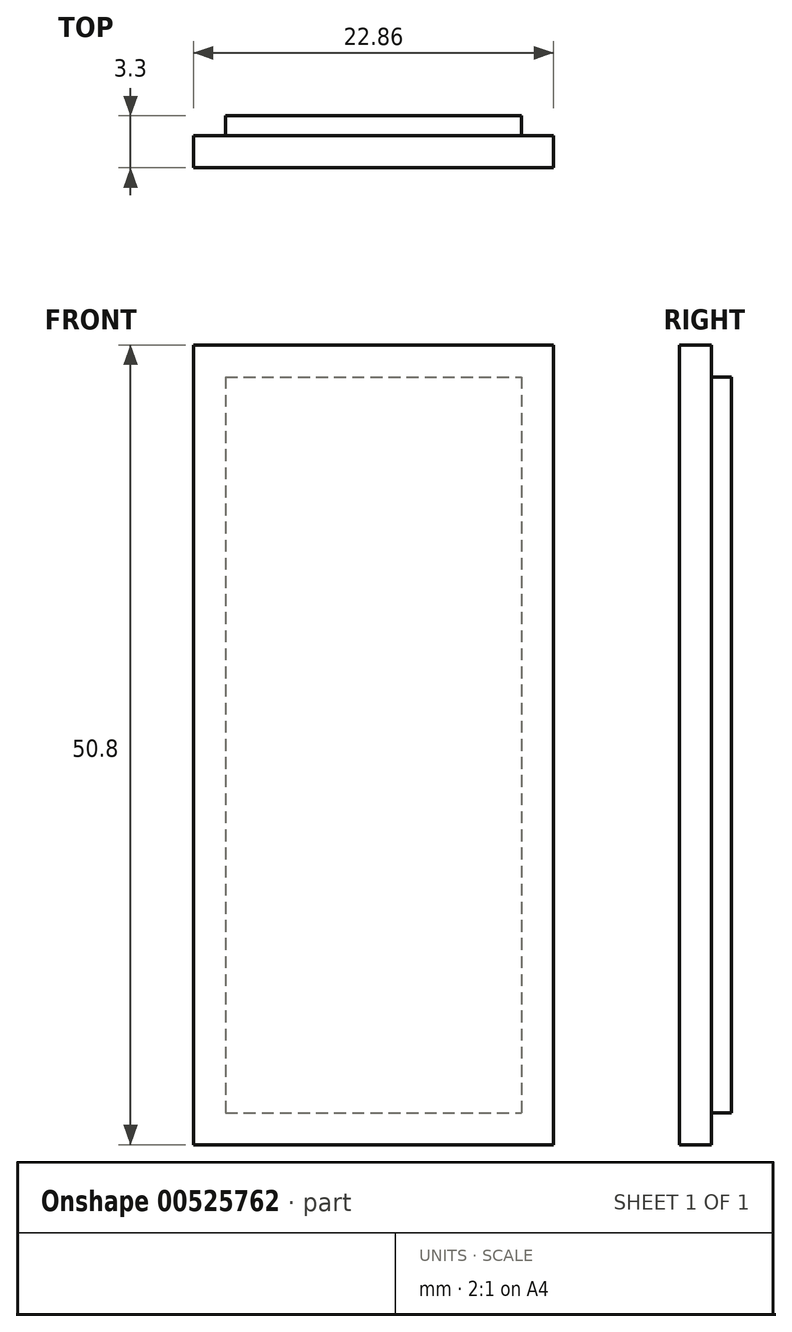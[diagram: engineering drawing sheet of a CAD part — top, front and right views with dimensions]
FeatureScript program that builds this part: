
annotation { "Feature Type Name" : "Feature", "Feature Type Description" : "" }
export const myFeature = defineFeature(function(context is Context, id is Id, definition is map)
    precondition{}
    {
        {
            var Q0;
            Q0=qCreatedBy(makeId("Front.planeOp"),FACE);
            var sketch = newSketch(context, id + "F0", { "sketchPlane" : qUnion([Q0])});
            skLineSegment(sketch, "E0.bottom", {"start": v(-6.63, 10.27) * mm, "end": v(16.23, 10.27) * mm});
            skLineSegment(sketch, "E0.top", {"start": v(-6.63, -40.53) * mm, "end": v(16.23, -40.53) * mm});
            skLineSegment(sketch, "E0.left", {"start": v(-6.63, 10.27) * mm, "end": v(-6.63, -40.53) * mm});
            skLineSegment(sketch, "E0.right", {"start": v(16.23, 10.27) * mm, "end": v(16.23, -40.53) * mm});
            skSolve(sketch);
        }
        {
            var Q0;
            Q0=makeQuery(id+"F0.imprint","IMPRINT",FACE,{"disambiguationData":[TD([[makeQuery(id+"F0.imprint","IMPRINT",EDGE,{"derivedFrom":sQuery(id+"F0.wireOp",EDGE,"E0.bottom")}),-1.0]])]});
            var sketch = newSketch(context, id + "F1", { "sketchPlane" : qUnion([Q0])});
            skLineSegment(sketch, "E1.bottom", {"start": v(-4.6, 8.24) * mm, "end": v(14.2, 8.24) * mm});
            skLineSegment(sketch, "E1.top", {"start": v(-4.6, -38.5) * mm, "end": v(14.2, -38.5) * mm});
            skLineSegment(sketch, "E1.left", {"start": v(-4.6, 8.24) * mm, "end": v(-4.6, -38.5) * mm});
            skLineSegment(sketch, "E1.right", {"start": v(14.2, 8.24) * mm, "end": v(14.2, -38.5) * mm});
            skSolve(sketch);
        }
        {
            var Q0;
            Q0=makeQuery(id+"F0.imprint","IMPRINT",FACE,{"disambiguationData":[TD([[makeQuery(id+"F0.imprint","IMPRINT",EDGE,{"derivedFrom":sQuery(id+"F0.wireOp",EDGE,"E0.bottom")}),-1.0]])]});
            extrude(context, id + "F2", {"entities" : qUnion([Q0]), "depth" : 2.03 * mm, "offsetDistance" : 25.4 * mm});
        }
        {
            var Q0;
            Q0=makeQuery(id+"F1.imprint","IMPRINT",FACE,{"disambiguationData":[TD([[makeQuery(id+"F1.imprint","IMPRINT",EDGE,{"derivedFrom":sQuery(id+"F1.wireOp",EDGE,"E1.bottom")}),-1.0]])]});
            extrude(context, id + "F3", {"entities" : qUnion([Q0]), "operationType" : NewBodyOperationType.ADD, "oppositeDirection" : true, "depth" : 1.27 * mm, "offsetDistance" : 25.4 * mm});
        }
    });
